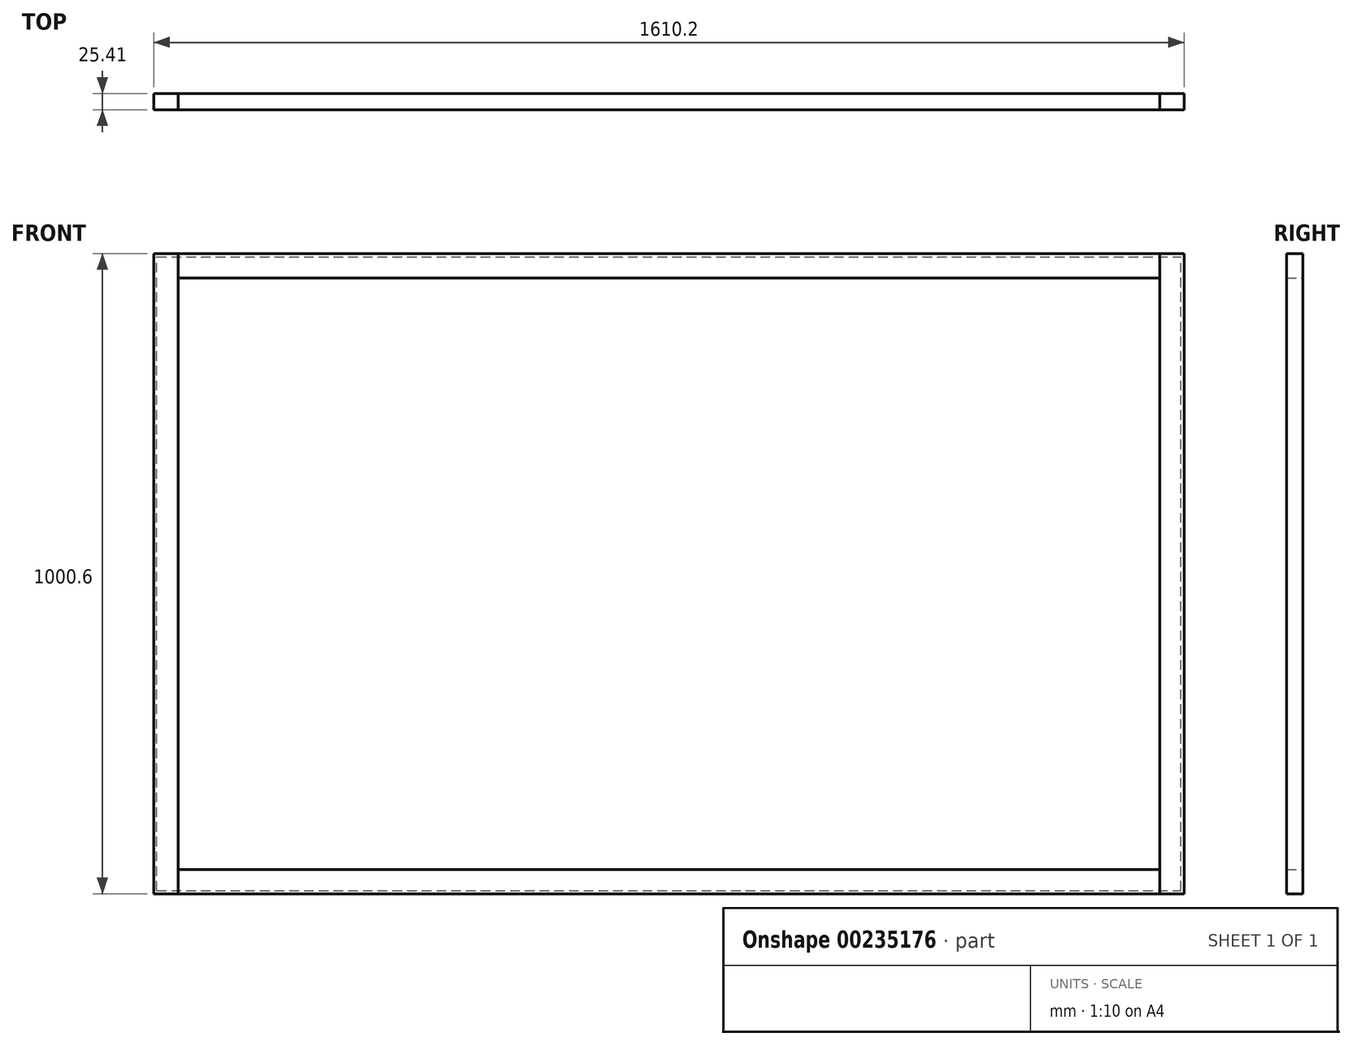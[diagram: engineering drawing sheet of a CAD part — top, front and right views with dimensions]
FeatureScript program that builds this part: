
annotation { "Feature Type Name" : "Feature", "Feature Type Description" : "" }
export const myFeature = defineFeature(function(context is Context, id is Id, definition is map)
    precondition{}
    {
        {
            assignVariable(context, id + "F0", {"name" : "frameThick", "anyValue" : 25.4 * mm});
        }
        {
            assignVariable(context, id + "F1", {"name" : "thick", "anyValue" : 3 / 203.2 * mm});
        }
        {
            var Q0;
            Q0=qCreatedBy(makeId("Front.planeOp"),FACE);
            var sketch = newSketch(context, id + "F2", { "sketchPlane" : qUnion([Q0])});
            skLineSegment(sketch, "E0.bottom", {"start": v(0, 0) * mm, "end": v(1600.2, 0) * mm});
            skLineSegment(sketch, "E0.top", {"start": v(0, 990.6) * mm, "end": v(1600.2, 990.6) * mm});
            skLineSegment(sketch, "E0.left", {"start": v(0, 0) * mm, "end": v(0, 990.6) * mm});
            skLineSegment(sketch, "E0.right", {"start": v(1600.2, 0) * mm, "end": v(1600.2, 990.6) * mm});
            skSolve(sketch);
        }
        {
            var Q0;
            Q0=makeQuery(id+"F2.imprint","IMPRINT",FACE,{"disambiguationData":[TD([[makeQuery(id+"F2.imprint","IMPRINT",EDGE,{"derivedFrom":sQuery(id+"F2.wireOp",EDGE,"E0.bottom")}),1.0]])]});
            extrude(context, id + "F3", {"entities" : qUnion([Q0]), "depth" : getVariable(context, 'thick')});
        }
        {
            var Q0;
            Q0=makeQuery(id+"F3.opExtrude","CAP_FACE",FACE,{"disambiguationData":[OSD([sQuery(id+"F2.wireOp",EDGE,"E0.bottom"),sQuery(id+"F2.wireOp",EDGE,"E0.top"),sQuery(id+"F2.wireOp",EDGE,"E0.left"),sQuery(id+"F2.wireOp",EDGE,"E0.right")])],"isStart":false});
            var sketch = newSketch(context, id + "F4", { "sketchPlane" : qUnion([Q0])});
            skLineSegment(sketch, "E1", {"start": v(800.1, 990.6) * mm, "end": v(800.1, 0) * mm, "construction": true});
            skLineSegment(sketch, "E2", {"start": v(0, 495.3) * mm, "end": v(1600.2, 495.3) * mm, "construction": true});
            skLineSegment(sketch, "E3.bottom", {"start": v(0, 990.6) * mm, "end": v(-5, 990.6) * mm, "construction": true});
            skLineSegment(sketch, "E3.top", {"start": v(0, 995.6) * mm, "end": v(-5, 995.6) * mm, "construction": true});
            skLineSegment(sketch, "E3.left", {"start": v(0, 990.6) * mm, "end": v(0, 995.6) * mm, "construction": true});
            skLineSegment(sketch, "E3.right", {"start": v(-5, 990.6) * mm, "end": v(-5, 995.6) * mm, "construction": true});
            skLineSegment(sketch, "E4.MirrorCS", {"start": v(1600.2, 995.6) * mm, "end": v(1605.2, 995.6) * mm, "construction": true});
            skLineSegment(sketch, "E5.MirrorCS", {"start": v(1600.2, 990.6) * mm, "end": v(1600.2, 995.6) * mm, "construction": true});
            skLineSegment(sketch, "E6.MirrorCS", {"start": v(1605.2, 990.6) * mm, "end": v(1605.2, 995.6) * mm, "construction": true});
            skLineSegment(sketch, "E7.MirrorCS", {"start": v(1600.2, 990.6) * mm, "end": v(1605.2, 990.6) * mm, "construction": true});
            skLineSegment(sketch, "E8.MirrorCS", {"start": v(0, 0) * mm, "end": v(-5, 0) * mm, "construction": true});
            skLineSegment(sketch, "E9.MirrorCS", {"start": v(0, -5) * mm, "end": v(-5, -5) * mm, "construction": true});
            skLineSegment(sketch, "E10.MirrorCS", {"start": v(0, 0) * mm, "end": v(0, -5) * mm, "construction": true});
            skLineSegment(sketch, "E11.MirrorCS", {"start": v(-5, 0) * mm, "end": v(-5, -5) * mm, "construction": true});
            skLineSegment(sketch, "E12.MirrorCS", {"start": v(1605.2, 0) * mm, "end": v(1605.2, -5) * mm, "construction": true});
            skLineSegment(sketch, "E13.MirrorCS", {"start": v(1600.2, 0) * mm, "end": v(1605.2, 0) * mm, "construction": true});
            skLineSegment(sketch, "E14.MirrorCS", {"start": v(1600.2, 0) * mm, "end": v(1600.2, -5) * mm, "construction": true});
            skLineSegment(sketch, "E15.MirrorCS", {"start": v(1600.2, -5) * mm, "end": v(1605.2, -5) * mm, "construction": true});
            skLineSegment(sketch, "E16.bottom", {"start": v(-5, 995.6) * mm, "end": v(33.1, 995.6) * mm});
            skLineSegment(sketch, "E16.top", {"start": v(-5, -5) * mm, "end": v(33.1, -5) * mm});
            skLineSegment(sketch, "E16.left", {"start": v(-5, 995.6) * mm, "end": v(-5, -5) * mm});
            skLineSegment(sketch, "E16.right", {"start": v(33.1, 995.6) * mm, "end": v(33.1, -5) * mm});
            skLineSegment(sketch, "E17.bottom", {"start": v(1605.2, 995.6) * mm, "end": v(1567.1, 995.6) * mm});
            skLineSegment(sketch, "E17.top", {"start": v(1605.2, -5) * mm, "end": v(1567.1, -5) * mm});
            skLineSegment(sketch, "E17.left", {"start": v(1605.2, 995.6) * mm, "end": v(1605.2, -5) * mm});
            skLineSegment(sketch, "E17.right", {"start": v(1567.1, 995.6) * mm, "end": v(1567.1, -5) * mm});
            skLineSegment(sketch, "E18.bottom", {"start": v(33.1, 995.6) * mm, "end": v(1567.1, 995.6) * mm});
            skLineSegment(sketch, "E18.top", {"start": v(33.1, 957.5) * mm, "end": v(1567.1, 957.5) * mm});
            skLineSegment(sketch, "E18.left", {"start": v(33.1, 995.6) * mm, "end": v(33.1, 957.5) * mm});
            skLineSegment(sketch, "E18.right", {"start": v(1567.1, 995.6) * mm, "end": v(1567.1, 957.5) * mm});
            skLineSegment(sketch, "E19.bottom", {"start": v(33.1, -5) * mm, "end": v(1567.1, -5) * mm});
            skLineSegment(sketch, "E19.top", {"start": v(33.1, 33.1) * mm, "end": v(1567.1, 33.1) * mm});
            skLineSegment(sketch, "E19.left", {"start": v(33.1, -5) * mm, "end": v(33.1, 33.1) * mm});
            skLineSegment(sketch, "E19.right", {"start": v(1567.1, -5) * mm, "end": v(1567.1, 33.1) * mm});
            skSolve(sketch);
        }
        {
            var Q0;
            {var subQ2=sQuery(id+"F4.wireOp",EDGE,"E16.right");Q0=makeQuery(id+"F4.imprint","IMPRINT",FACE,{"disambiguationData":[TD([[makeQuery(id+"F4.imprint","IMPRINT",EDGE,{"derivedFrom":subQ2}),-1.0]])]});}
            var Q1;
            {var subQ1=sQuery(id+"F4.wireOp",EDGE,"E16.bottom");Q1=makeQuery(id+"F4.imprint","IMPRINT",FACE,{"disambiguationData":[TD([[makeQuery(id+"F4.imprint","IMPRINT",EDGE,{"derivedFrom":subQ1}),-1.0]])]});}
            extrude(context, id + "F5", {"entities" : qUnion([Q0, Q1]), "depth" : getVariable(context, 'frameThick')});
        }
        {
            var Q0;
            {var subQ0=sQuery(id+"F4.wireOp",EDGE,"E18.top");Q0=makeQuery(id+"F4.imprint","IMPRINT",FACE,{"disambiguationData":[TD([[makeQuery(id+"F4.imprint","IMPRINT",EDGE,{"derivedFrom":subQ0}),1.0]])]});}
            var Q1;
            {var subQ0=sQuery(id+"F4.wireOp",EDGE,"E18.bottom");Q1=makeQuery(id+"F4.imprint","IMPRINT",FACE,{"disambiguationData":[TD([[makeQuery(id+"F4.imprint","IMPRINT",EDGE,{"derivedFrom":subQ0}),-1.0]])]});}
            extrude(context, id + "F6", {"entities" : qUnion([Q0, Q1]), "depth" : getVariable(context, 'frameThick')});
        }
        {
            var Q0;
            {var subQ2=sQuery(id+"F4.wireOp",EDGE,"E17.right");Q0=makeQuery(id+"F4.imprint","IMPRINT",FACE,{"disambiguationData":[TD([[makeQuery(id+"F4.imprint","IMPRINT",EDGE,{"derivedFrom":subQ2}),1.0]])]});}
            var Q1;
            {var subQ1=sQuery(id+"F4.wireOp",EDGE,"E17.bottom");Q1=makeQuery(id+"F4.imprint","IMPRINT",FACE,{"disambiguationData":[TD([[makeQuery(id+"F4.imprint","IMPRINT",EDGE,{"derivedFrom":subQ1}),1.0]])]});}
            extrude(context, id + "F7", {"entities" : qUnion([Q0, Q1]), "depth" : getVariable(context, 'frameThick')});
        }
        {
            var Q0;
            {var subQ0=sQuery(id+"F4.wireOp",EDGE,"E19.top");Q0=makeQuery(id+"F4.imprint","IMPRINT",FACE,{"disambiguationData":[TD([[makeQuery(id+"F4.imprint","IMPRINT",EDGE,{"derivedFrom":subQ0}),-1.0]])]});}
            var Q1;
            {var subQ0=sQuery(id+"F4.wireOp",EDGE,"E19.bottom");Q1=makeQuery(id+"F4.imprint","IMPRINT",FACE,{"disambiguationData":[TD([[makeQuery(id+"F4.imprint","IMPRINT",EDGE,{"derivedFrom":subQ0}),1.0]])]});}
            extrude(context, id + "F8", {"entities" : qUnion([Q0, Q1]), "depth" : getVariable(context, 'frameThick')});
        }
    });
